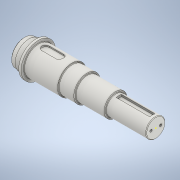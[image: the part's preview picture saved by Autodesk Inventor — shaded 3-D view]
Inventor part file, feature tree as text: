
AUTODESK INVENTOR PART (.ipt)
format: ipt  version: 2020 (Build 240168000, 168)  size: 261,120 bytes
history: native  units: mm
features: sketch x5, other x4, extrude x3, projected_geometry x2, revolve x1, chamfer x1, fillet x1, hole x1, plane x1
ambient origin geometry x6: Origin, XZ Plane, XY Plane, X Axis, Y Axis, Z Axis
bodies: 实体1 (feature_tree)
feature tree (19):
  revolve  "旋转1"  [1 undecoded]
  other  "键槽1"
  extrude  "拉伸4"  Depth=144.0mm
  extrude  "拉伸5"  Depth=110.0mm
  chamfer  "倒角1"  [1 undecoded]
  fillet  "圆角1"  Radius=19.0mm
  sketch  "草图8"  dims[d6=120.0mm d7=110.0mm]
  hole  "孔1"  [1 undecoded]
  plane  "工作平面1"
  extrude  "拉伸6"  Depth=2.0mm TaperAngle=45.0deg
  other  "起始平面"
  other  "主草图"
  other  "iFeature3:1"
  sketch  "草图6"  dims[d0=0.0mm d1=0.0mm d2=0.0mm d3=110.0mm]
  projected_geometry  "投影回路3"
  sketch  "草图7"  dims[d4=116.0mm d5=144.0mm]
  projected_geometry  "投影回路4"
  sketch  "草图9"  dims[d8=96.0mm]
  sketch  "草图10"  dims[d9=80.0mm d10=0.0mm d20=19.0mm d21=0.0mm d22=30.0mm d23=0.0mm d24=2.5mm d25=2.0mm d26=45.0deg d27=2.0mm d28=40.0mm d29=10.106mm d30=20.0mm d31=4.0mm d32=2.0mm d33=90.0deg d34=25.0mm d35=20.594885mm d36=140.0mm d37=22.0mm d38=14.0mm d39=9.0mm d40=0.0mm]
note: 3 required parameter values undecoded (feature->parameter linkage not recoverable at this tier; creation-order binding heuristic only, values carry confidence <= 0.55)